# Revit family: 4460_Addressable 230VAC Relay Output Unit
name_source: partatom
category: Fire Alarm Devices
units: mm (PartAtom-declared; Revit-internal decimal feet)

## family parameters
Cut with Voids When Loaded = No
Host = Face
Maintain Annotation Orientation = No
OmniClass Number = 23.85.30.21
OmniClass Title = Environmental Detection/Registration
Part Type = Normal
Room Calculation Point = No
Round Connector Dimension = Use Diameter
Shared = No

## types (1)
- 4460
    Ambient Humidity = Maximum 95 % RH
    Ambient Temperature Operating = -10 to +50 °C
    Ambient Temperature Storage = -20 to +60 °C
    CPR = -
    Current (Active) = ≤ 1.7 mA
    Current Quiescent = ≤ 1.7 mA
    Default Elevation = 0 mm  [stored 0 ft]
    Depth (mm) = 60 mm  [stored 0.19685 ft]
    Description = Addressable 2 inputs unit with isolator 4460
    Enclosure = Standard Fibox encapsulation. (PCM 125/60 G)
    Height (mm) = 130 mm  [stored 0.426509 ft]
    Ingress Protection Rating = IP66/67
    Manufacturer = Panasonic
    Max. Switching Capacity = 8A 250 V AC (resistive load) / 8A 30 V DC (resistive load)
    Max_Wire Size = J1 Ø 1.7 mm (2.5 mm²) / J2 Ø 2.2 mm (4 mm²)
    Min_Wire Size = J1 Ø 0.5 mm (0.2 mm²) / J2 Ø 0.5 mm (0.2 mm²)
    Model = 4460
    Omniclass Code = 23.85.30.21.11.11.11
    Omniclass Description = Smoke Detectors
    Power Supply = Via COM loop
    Product Material = Polycarbonate_Panasonic_White
    Relay Outputs = 1
    Short Circuit Isolator = Yes (Built-in)
    Tested and Approved = EN54-18, EN54-17
    Type Comments = The 4460 is a dual input unit with isolator for monitoring of various equipment like switches, sprinkler valves, etc. The inputs are programmed via EBLWin. NC or NO contact.
    URL = https://www.panasonic-fire-security.com
    Uniclass 2015 Code = Pr_75_80_30_27
    Uniclass 2015 Description = Fire and smoke detector bases
    Uniformat 2010  Code = D7050
    Uniformat 2010 Description = Detection and Alarm
    Version = RVT20
    Voltage Allowed = 12 – 30 VDC
    Voltage Normal = 24 VDC
    Weight = 250g
    Width (mm) = 130 mm  [stored 0.426509 ft]

note: [stored X ft] marks values corroborated as IEEE doubles in the binary element streams (Revit-internal decimal feet)

## geometry (parser evidence)
native form markers: Blend x86, Sweep x2
no freeform markers — native parametric forms only
